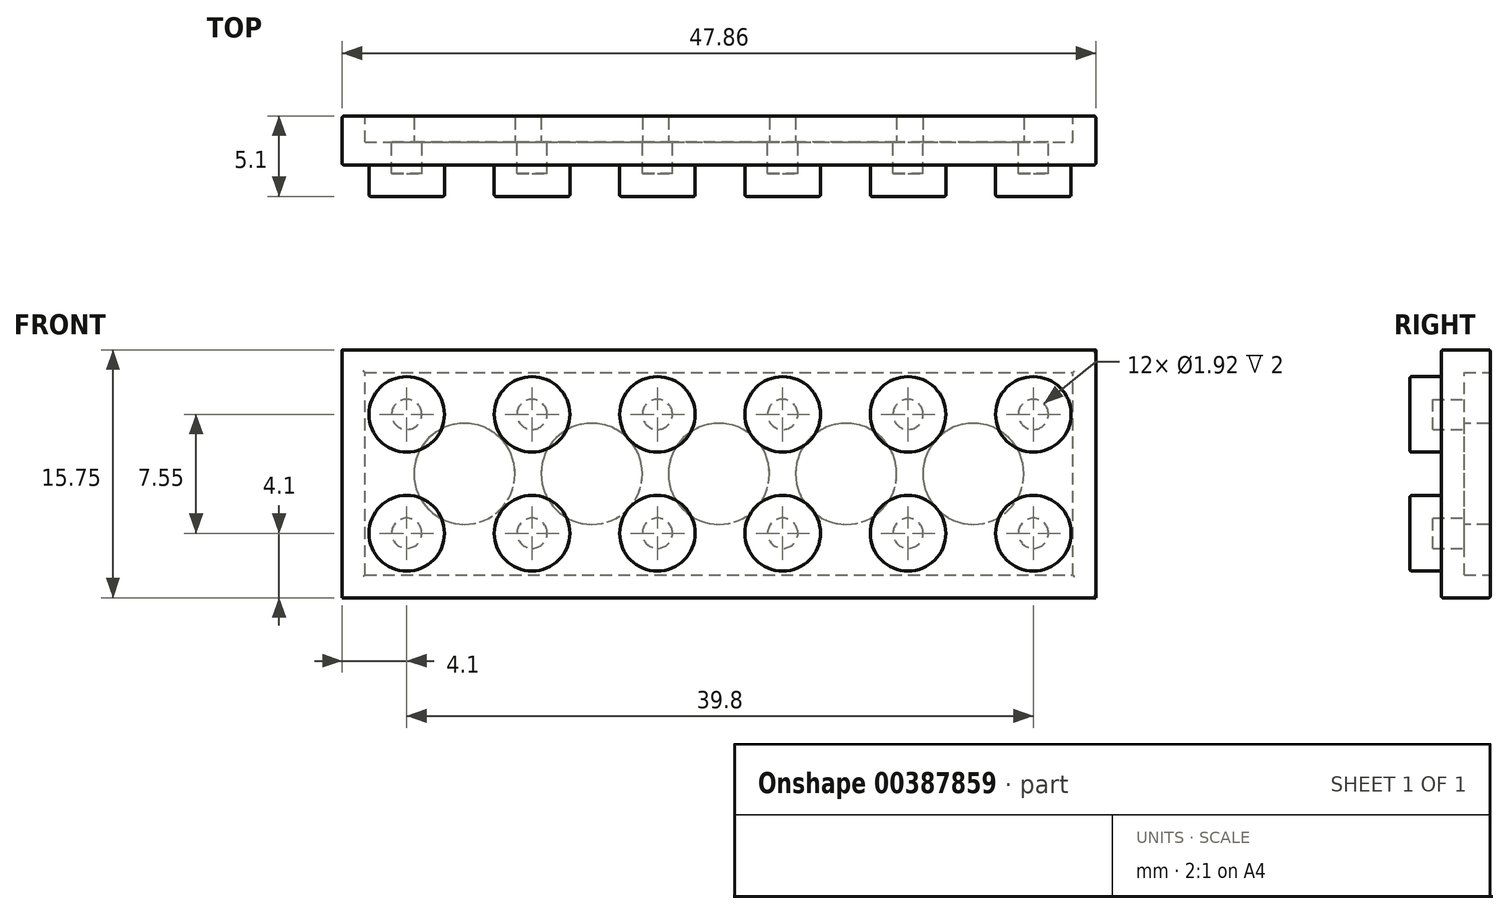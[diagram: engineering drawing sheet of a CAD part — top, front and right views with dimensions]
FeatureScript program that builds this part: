
annotation { "Feature Type Name" : "Feature", "Feature Type Description" : "" }
export const myFeature = defineFeature(function(context is Context, id is Id, definition is map)
    precondition{}
    {
        {
            var Q0;
            Q0=qCreatedBy(makeId("Front.planeOp"),FACE);
            var sketch = newSketch(context, id + "F0", { "sketchPlane" : qUnion([Q0])});
            skLineSegment(sketch, "E0.bottom", {"start": v(0, 0) * mm, "end": v(47.86, 0) * mm});
            skLineSegment(sketch, "E0.top", {"start": v(0, 15.75) * mm, "end": v(47.86, 15.75) * mm});
            skLineSegment(sketch, "E0.left", {"start": v(0, 0) * mm, "end": v(0, 15.75) * mm});
            skLineSegment(sketch, "E0.right", {"start": v(47.86, 0) * mm, "end": v(47.86, 15.75) * mm});
            skSolve(sketch);
        }
        {
            var Q0;
            Q0=makeQuery(id+"F0.imprint","IMPRINT",FACE,{"disambiguationData":[TD([[makeQuery(id+"F0.imprint","IMPRINT",EDGE,{"derivedFrom":sQuery(id+"F0.wireOp",EDGE,"E0.bottom")}),1.0]])]});
            extrude(context, id + "F1", {"entities" : qUnion([Q0]), "depth" : 3.09 * mm});
        }
        {
            var Q0;
            Q0=makeQuery(id+"F1.opExtrude","CAP_FACE",FACE,{"disambiguationData":[OSD([sQuery(id+"F0.wireOp",EDGE,"E0.bottom"),sQuery(id+"F0.wireOp",EDGE,"E0.top"),sQuery(id+"F0.wireOp",EDGE,"E0.left"),sQuery(id+"F0.wireOp",EDGE,"E0.right")])],"isStart":false});
            var sketch = newSketch(context, id + "F2", { "sketchPlane" : qUnion([Q0])});
            skCircle(sketch, "E1", {"center": v(4.1, 11.65) * mm, "radius": 2.4 * mm});
            skSolve(sketch);
        }
        {
            var Q0;
            Q0=makeQuery(id+"F2.imprint","IMPRINT",FACE,{"disambiguationData":[TD([[makeQuery(id+"F2.imprint","IMPRINT",EDGE,{"derivedFrom":sQuery(id+"F2.wireOp",EDGE,"E1")}),1.0]])]});
            extrude(context, id + "F3", {"entities" : qUnion([Q0]), "operationType" : NewBodyOperationType.ADD, "depth" : 2 * mm});
        }
        {
            var Q0;
            Q0=makeQuery(id+"F1.opExtrude","CAP_FACE",FACE,{"disambiguationData":[OSD([sQuery(id+"F0.wireOp",EDGE,"E0.bottom"),sQuery(id+"F0.wireOp",EDGE,"E0.top"),sQuery(id+"F0.wireOp",EDGE,"E0.left"),sQuery(id+"F0.wireOp",EDGE,"E0.right")])],"isStart":false});
            var sketch = newSketch(context, id + "F4", { "sketchPlane" : qUnion([Q0])});
            skCircle(sketch, "E2", {"center": v(4.1, 4.1) * mm, "radius": 2.4 * mm});
            skSolve(sketch);
        }
        {
            var Q0;
            Q0=qSketchRegion(id+"F4",true);
            extrude(context, id + "F5", {"entities" : qUnion([Q0]), "operationType" : NewBodyOperationType.ADD, "depth" : 2 * mm});
        }
        {
            var Q0;
            Q0=makeQuery(id+"F1.opExtrude","CAP_FACE",FACE,{"disambiguationData":[OSD([sQuery(id+"F0.wireOp",EDGE,"E0.bottom"),sQuery(id+"F0.wireOp",EDGE,"E0.top"),sQuery(id+"F0.wireOp",EDGE,"E0.left"),sQuery(id+"F0.wireOp",EDGE,"E0.right")])],"isStart":false});
            var sketch = newSketch(context, id + "F6", { "sketchPlane" : qUnion([Q0])});
            skCircle(sketch, "E3", {"center": v(12.06, 11.65) * mm, "radius": 2.4 * mm});
            skSolve(sketch);
        }
        {
            var Q0;
            Q0=qSketchRegion(id+"F6",true);
            extrude(context, id + "F7", {"entities" : qUnion([Q0]), "operationType" : NewBodyOperationType.ADD, "depth" : 2 * mm});
        }
        {
            var Q0;
            Q0=makeQuery(id+"F1.opExtrude","CAP_FACE",FACE,{"disambiguationData":[OSD([sQuery(id+"F0.wireOp",EDGE,"E0.bottom"),sQuery(id+"F0.wireOp",EDGE,"E0.top"),sQuery(id+"F0.wireOp",EDGE,"E0.left"),sQuery(id+"F0.wireOp",EDGE,"E0.right")])],"isStart":false});
            var sketch = newSketch(context, id + "F8", { "sketchPlane" : qUnion([Q0])});
            skCircle(sketch, "E4", {"center": v(12.06, 4.1) * mm, "radius": 2.4 * mm});
            skSolve(sketch);
        }
        {
            var Q0;
            Q0=qSketchRegion(id+"F8",true);
            extrude(context, id + "F9", {"entities" : qUnion([Q0]), "operationType" : NewBodyOperationType.ADD, "depth" : 2 * mm});
        }
        {
            var Q0;
            Q0=makeQuery(id+"F1.opExtrude","CAP_FACE",FACE,{"disambiguationData":[OSD([sQuery(id+"F0.wireOp",EDGE,"E0.bottom"),sQuery(id+"F0.wireOp",EDGE,"E0.top"),sQuery(id+"F0.wireOp",EDGE,"E0.left"),sQuery(id+"F0.wireOp",EDGE,"E0.right")])],"isStart":false});
            var sketch = newSketch(context, id + "F10", { "sketchPlane" : qUnion([Q0])});
            skCircle(sketch, "E5", {"center": v(20.02, 11.65) * mm, "radius": 2.4 * mm});
            skSolve(sketch);
        }
        {
            var Q0;
            Q0=qSketchRegion(id+"F10",true);
            extrude(context, id + "F11", {"entities" : qUnion([Q0]), "operationType" : NewBodyOperationType.ADD, "depth" : 2 * mm});
        }
        {
            var Q0;
            Q0=makeQuery(id+"F1.opExtrude","CAP_FACE",FACE,{"disambiguationData":[OSD([sQuery(id+"F0.wireOp",EDGE,"E0.bottom"),sQuery(id+"F0.wireOp",EDGE,"E0.top"),sQuery(id+"F0.wireOp",EDGE,"E0.left"),sQuery(id+"F0.wireOp",EDGE,"E0.right")])],"isStart":false});
            var sketch = newSketch(context, id + "F12", { "sketchPlane" : qUnion([Q0])});
            skCircle(sketch, "E6", {"center": v(20.02, 4.1) * mm, "radius": 2.4 * mm});
            skSolve(sketch);
        }
        {
            var Q0;
            Q0=qSketchRegion(id+"F12",true);
            extrude(context, id + "F13", {"entities" : qUnion([Q0]), "operationType" : NewBodyOperationType.ADD, "depth" : 2 * mm});
        }
        {
            var Q0;
            Q0=makeQuery(id+"F1.opExtrude","CAP_FACE",FACE,{"disambiguationData":[OSD([sQuery(id+"F0.wireOp",EDGE,"E0.bottom"),sQuery(id+"F0.wireOp",EDGE,"E0.top"),sQuery(id+"F0.wireOp",EDGE,"E0.left"),sQuery(id+"F0.wireOp",EDGE,"E0.right")])],"isStart":false});
            var sketch = newSketch(context, id + "F14", { "sketchPlane" : qUnion([Q0])});
            skCircle(sketch, "E7", {"center": v(27.98, 11.65) * mm, "radius": 2.4 * mm});
            skSolve(sketch);
        }
        {
            var Q0;
            Q0=qSketchRegion(id+"F14",true);
            extrude(context, id + "F15", {"entities" : qUnion([Q0]), "operationType" : NewBodyOperationType.ADD, "depth" : 2 * mm});
        }
        {
            var Q0;
            Q0=makeQuery(id+"F1.opExtrude","CAP_FACE",FACE,{"disambiguationData":[OSD([sQuery(id+"F0.wireOp",EDGE,"E0.bottom"),sQuery(id+"F0.wireOp",EDGE,"E0.top"),sQuery(id+"F0.wireOp",EDGE,"E0.left"),sQuery(id+"F0.wireOp",EDGE,"E0.right")])],"isStart":false});
            var sketch = newSketch(context, id + "F16", { "sketchPlane" : qUnion([Q0])});
            skCircle(sketch, "E8", {"center": v(27.98, 4.1) * mm, "radius": 2.4 * mm});
            skSolve(sketch);
        }
        {
            var Q0;
            Q0=qSketchRegion(id+"F16",true);
            extrude(context, id + "F17", {"entities" : qUnion([Q0]), "operationType" : NewBodyOperationType.ADD, "depth" : 2 * mm});
        }
        {
            var Q0;
            Q0=makeQuery(id+"F1.opExtrude","CAP_FACE",FACE,{"disambiguationData":[OSD([sQuery(id+"F0.wireOp",EDGE,"E0.bottom"),sQuery(id+"F0.wireOp",EDGE,"E0.top"),sQuery(id+"F0.wireOp",EDGE,"E0.left"),sQuery(id+"F0.wireOp",EDGE,"E0.right")])],"isStart":false});
            var sketch = newSketch(context, id + "F18", { "sketchPlane" : qUnion([Q0])});
            skCircle(sketch, "E9", {"center": v(35.94, 11.65) * mm, "radius": 2.4 * mm});
            skSolve(sketch);
        }
        {
            var Q0;
            Q0=qSketchRegion(id+"F18",true);
            extrude(context, id + "F19", {"entities" : qUnion([Q0]), "operationType" : NewBodyOperationType.ADD, "depth" : 2 * mm});
        }
        {
            var Q0;
            Q0=makeQuery(id+"F1.opExtrude","CAP_FACE",FACE,{"disambiguationData":[OSD([sQuery(id+"F0.wireOp",EDGE,"E0.bottom"),sQuery(id+"F0.wireOp",EDGE,"E0.top"),sQuery(id+"F0.wireOp",EDGE,"E0.left"),sQuery(id+"F0.wireOp",EDGE,"E0.right")])],"isStart":false});
            var sketch = newSketch(context, id + "F20", { "sketchPlane" : qUnion([Q0])});
            skCircle(sketch, "E10", {"center": v(35.94, 4.1) * mm, "radius": 2.4 * mm});
            skSolve(sketch);
        }
        {
            var Q0;
            Q0=qSketchRegion(id+"F20",true);
            extrude(context, id + "F21", {"entities" : qUnion([Q0]), "operationType" : NewBodyOperationType.ADD, "depth" : 2 * mm});
        }
        {
            var Q0;
            Q0=makeQuery(id+"F1.opExtrude","CAP_FACE",FACE,{"disambiguationData":[OSD([sQuery(id+"F0.wireOp",EDGE,"E0.bottom"),sQuery(id+"F0.wireOp",EDGE,"E0.top"),sQuery(id+"F0.wireOp",EDGE,"E0.left"),sQuery(id+"F0.wireOp",EDGE,"E0.right")])],"isStart":false});
            var sketch = newSketch(context, id + "F22", { "sketchPlane" : qUnion([Q0])});
            skCircle(sketch, "E11", {"center": v(43.9, 11.65) * mm, "radius": 2.4 * mm});
            skCircle(sketch, "E12", {"center": v(42.7, 3.96) * mm, "radius": 2.55 * mm});
            skSolve(sketch);
        }
        {
            var Q0;
            Q0=makeQuery(id+"F22.imprint","IMPRINT",FACE,{"disambiguationData":[TD([[makeQuery(id+"F22.imprint","IMPRINT",EDGE,{"derivedFrom":sQuery(id+"F22.wireOp",EDGE,"E11")}),1.0]])]});
            extrude(context, id + "F23", {"entities" : qUnion([Q0]), "operationType" : NewBodyOperationType.ADD, "depth" : 2 * mm});
        }
        {
            var Q0;
            Q0=makeQuery(id+"F1.opExtrude","CAP_FACE",FACE,{"disambiguationData":[OSD([sQuery(id+"F0.wireOp",EDGE,"E0.bottom"),sQuery(id+"F0.wireOp",EDGE,"E0.top"),sQuery(id+"F0.wireOp",EDGE,"E0.left"),sQuery(id+"F0.wireOp",EDGE,"E0.right")])],"isStart":false});
            var sketch = newSketch(context, id + "F24", { "sketchPlane" : qUnion([Q0])});
            skCircle(sketch, "E13", {"center": v(43.9, 4.1) * mm, "radius": 2.4 * mm});
            skSolve(sketch);
        }
        {
            var Q0;
            Q0=qSketchRegion(id+"F24",true);
            extrude(context, id + "F25", {"entities" : qUnion([Q0]), "operationType" : NewBodyOperationType.ADD, "depth" : 2 * mm});
        }
        {
            var Q0;
            Q0=makeQuery(id+"F1.opExtrude","CAP_FACE",FACE,{"disambiguationData":[OSD([sQuery(id+"F0.wireOp",EDGE,"E0.bottom"),sQuery(id+"F0.wireOp",EDGE,"E0.top"),sQuery(id+"F0.wireOp",EDGE,"E0.left"),sQuery(id+"F0.wireOp",EDGE,"E0.right")])],"isStart":true});
            shell(context, id + "F26", {"entities" : qUnion([Q0]), "thickness" : 1.44 * mm});
        }
        {
            var Q0;
            Q0=makeQuery(id+"F26.opShell","OFFSET_FACE",FACE,{"disambiguationData":[OSD([sQuery(id+"F0.wireOp",EDGE,"E0.bottom"),sQuery(id+"F0.wireOp",EDGE,"E0.top"),sQuery(id+"F0.wireOp",EDGE,"E0.left"),sQuery(id+"F0.wireOp",EDGE,"E0.right")])]});
            var sketch = newSketch(context, id + "F27", { "sketchPlane" : qUnion([Q0])});
            skCircle(sketch, "E14", {"center": v(-23.93, 7.88) * mm, "radius": 3.2 * mm});
            skPoint(sketch, "E14.centerSnap0", {"position": v(-23.93, 1.44) * mm});
            skPoint(sketch, "E14.centerSnap1", {"position": v(-1.44, 7.88) * mm});
            skCircle(sketch, "E15", {"center": v(-7.77, 7.88) * mm, "radius": 3.2 * mm});
            skCircle(sketch, "E16", {"center": v(-15.85, 7.88) * mm, "radius": 3.2 * mm});
            skCircle(sketch, "E17", {"center": v(-32, 7.88) * mm, "radius": 3.2 * mm});
            skCircle(sketch, "E18", {"center": v(-40.1, 7.88) * mm, "radius": 3.2 * mm});
            skSolve(sketch);
        }
        {
            var Q0;
            Q0=qSketchRegion(id+"F27",true);
            extrude(context, id + "F28", {"entities" : qUnion([Q0]), "operationType" : NewBodyOperationType.ADD, "depth" : 1.66 * mm});
        }
        {
            var Q0;
            Q0=makeQuery(id+"F3.opExtrude","CAP_EDGE",EDGE,{"disambiguationData":[OSD([sQuery(id+"F2.wireOp",EDGE,"E1")])],"isStart":false});
            var Q1;
            Q1=makeQuery(id+"F7.opExtrude","CAP_EDGE",EDGE,{"disambiguationData":[OSD([sQuery(id+"F6.wireOp",EDGE,"E3")])],"isStart":false});
            var Q2;
            Q2=makeQuery(id+"F11.opExtrude","CAP_EDGE",EDGE,{"disambiguationData":[OSD([sQuery(id+"F10.wireOp",EDGE,"E5")])],"isStart":false});
            var Q3;
            Q3=makeQuery(id+"F15.opExtrude","CAP_EDGE",EDGE,{"disambiguationData":[OSD([sQuery(id+"F14.wireOp",EDGE,"E7")])],"isStart":false});
            var Q4;
            Q4=makeQuery(id+"F19.opExtrude","CAP_EDGE",EDGE,{"disambiguationData":[OSD([sQuery(id+"F18.wireOp",EDGE,"E9")])],"isStart":false});
            var Q5;
            Q5=makeQuery(id+"F23.opExtrude","CAP_EDGE",EDGE,{"disambiguationData":[OSD([sQuery(id+"F22.wireOp",EDGE,"E11")])],"isStart":false});
            var Q6;
            Q6=makeQuery(id+"F25.opExtrude","CAP_EDGE",EDGE,{"disambiguationData":[OSD([sQuery(id+"F24.wireOp",EDGE,"E13")])],"isStart":false});
            var Q7;
            Q7=makeQuery(id+"F21.opExtrude","CAP_EDGE",EDGE,{"disambiguationData":[OSD([sQuery(id+"F20.wireOp",EDGE,"E10")])],"isStart":false});
            var Q8;
            Q8=makeQuery(id+"F17.opExtrude","CAP_EDGE",EDGE,{"disambiguationData":[OSD([sQuery(id+"F16.wireOp",EDGE,"E8")])],"isStart":false});
            var Q9;
            Q9=makeQuery(id+"F13.opExtrude","CAP_EDGE",EDGE,{"disambiguationData":[OSD([sQuery(id+"F12.wireOp",EDGE,"E6")])],"isStart":false});
            var Q10;
            Q10=makeQuery(id+"F9.opExtrude","CAP_EDGE",EDGE,{"disambiguationData":[OSD([sQuery(id+"F8.wireOp",EDGE,"E4")])],"isStart":false});
            var Q11;
            Q11=makeQuery(id+"F5.opExtrude","CAP_EDGE",EDGE,{"disambiguationData":[OSD([sQuery(id+"F4.wireOp",EDGE,"E2")])],"isStart":false});
            var Q12;
            Q12=makeQuery(id+"F1.opExtrude","CAP_FACE",FACE,{"disambiguationData":[OSD([sQuery(id+"F0.wireOp",EDGE,"E0.bottom"),sQuery(id+"F0.wireOp",EDGE,"E0.top"),sQuery(id+"F0.wireOp",EDGE,"E0.left"),sQuery(id+"F0.wireOp",EDGE,"E0.right")])],"isStart":false});
            fillet(context, id + "F29", {"entities" : qUnion([Q0, Q1, Q2, Q3, Q4, Q5, Q6, Q7, Q8, Q9, Q10, Q11, Q12]), "radius" : .1 * mm, "tangentPropagation" : true, "allowEdgeOverflow" : false});
        }
        {
            var Q0;
            {var subQ0=sQuery(id+"F0.wireOp",EDGE,"E0.bottom");Q0=makeQuery(id+"F26.opShell","OFFSET_EDGE",EDGE,{"disambiguationData":[OSD([subQ0]),TDD([makeQuery(id+"F1.opExtrude","CAP_EDGE",EDGE,{"disambiguationData":[OSD([subQ0])],"isStart":true})])]});}
            var Q1;
            Q1=makeQuery(id+"F1.opExtrude","CAP_FACE",FACE,{"disambiguationData":[OSD([sQuery(id+"F0.wireOp",EDGE,"E0.bottom"),sQuery(id+"F0.wireOp",EDGE,"E0.top"),sQuery(id+"F0.wireOp",EDGE,"E0.left"),sQuery(id+"F0.wireOp",EDGE,"E0.right")])],"isStart":true});
            var Q2;
            Q2=makeQuery(id+"F28.opExtrude","CAP_EDGE",EDGE,{"disambiguationData":[OSD([sQuery(id+"F27.wireOp",EDGE,"E15")])],"isStart":false});
            var Q3;
            Q3=makeQuery(id+"F28.opExtrude","CAP_FACE",FACE,{"disambiguationData":[OSD([sQuery(id+"F27.wireOp",EDGE,"E16")])],"isStart":false});
            var Q4;
            Q4=makeQuery(id+"F28.opExtrude","CAP_FACE",FACE,{"disambiguationData":[OSD([sQuery(id+"F27.wireOp",EDGE,"E14")])],"isStart":false});
            var Q5;
            Q5=makeQuery(id+"F28.opExtrude","CAP_EDGE",EDGE,{"disambiguationData":[OSD([sQuery(id+"F27.wireOp",EDGE,"E17")])],"isStart":false});
            var Q6;
            Q6=makeQuery(id+"F28.opExtrude","CAP_EDGE",EDGE,{"disambiguationData":[OSD([sQuery(id+"F27.wireOp",EDGE,"E18")])],"isStart":false});
            fillet(context, id + "F30", {"entities" : qUnion([Q0, Q1, Q2, Q3, Q4, Q5, Q6]), "radius" : .1 * mm, "tangentPropagation" : true, "allowEdgeOverflow" : false});
        }
    });
